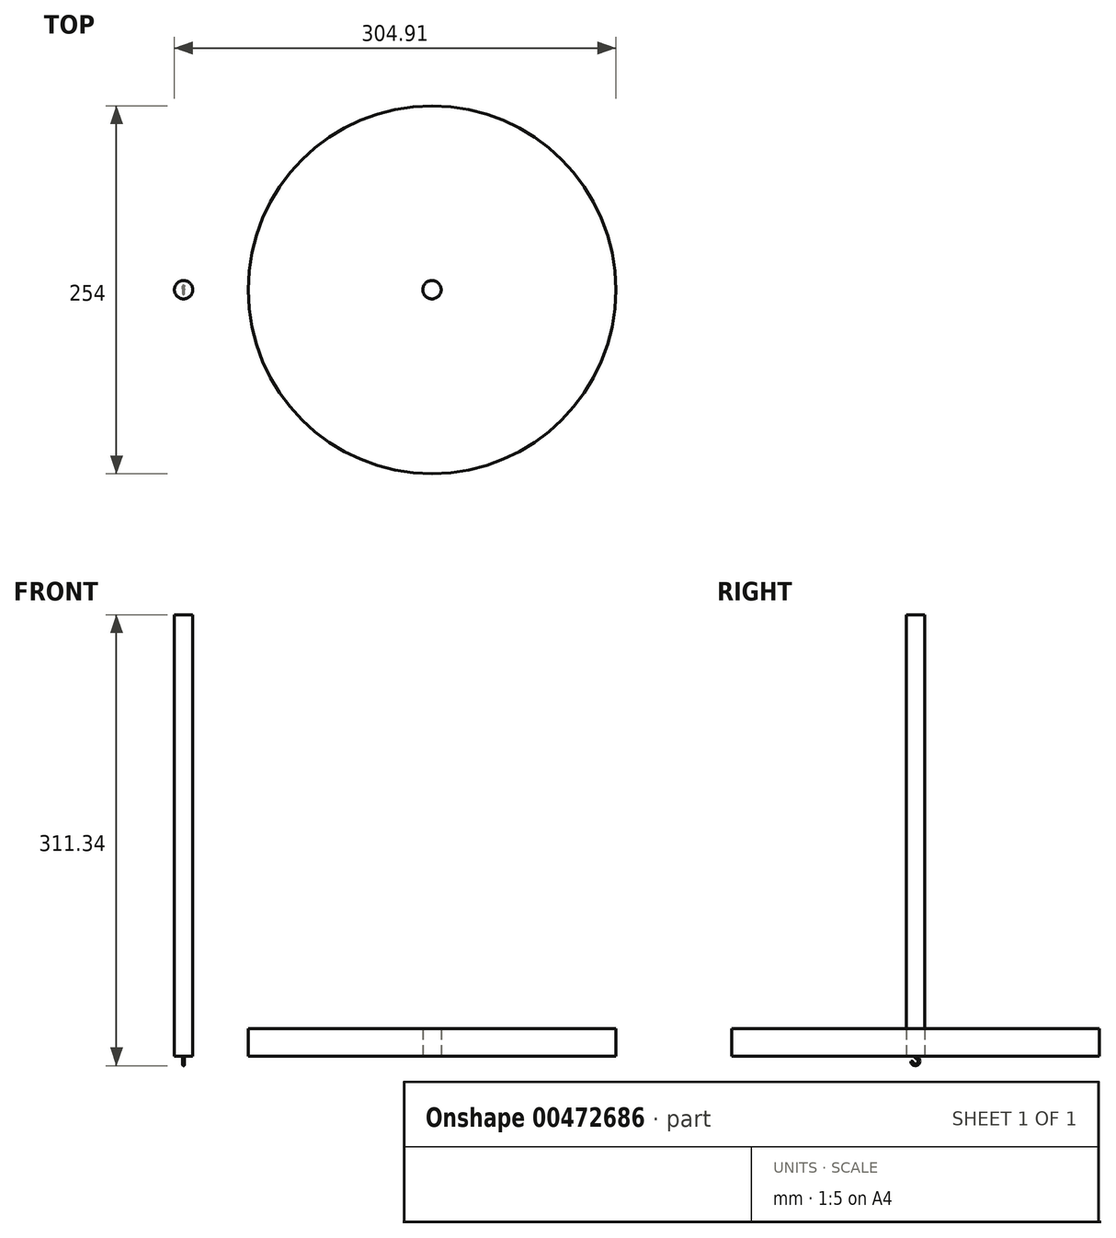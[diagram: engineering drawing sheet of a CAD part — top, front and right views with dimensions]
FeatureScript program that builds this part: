
annotation { "Feature Type Name" : "Feature", "Feature Type Description" : "" }
export const myFeature = defineFeature(function(context is Context, id is Id, definition is map)
    precondition{}
    {
        {
            var Q0;
            Q0=qCreatedBy(makeId("Top.planeOp"),FACE);
            var sketch = newSketch(context, id + "F0", { "sketchPlane" : qUnion([Q0])});
            skCircle(sketch, "E0", {"center": v(0, 0) * mm, "radius": 6.35 * mm});
            skCircle(sketch, "E1", {"center": v(171.56, 0) * mm, "radius": 127 * mm});
            skCircle(sketch, "E2", {"center": v(171.56, 0) * mm, "radius": 6.35 * mm});
            skSolve(sketch);
        }
        {
            var Q0;
            Q0=makeQuery(id+"F0.imprint","IMPRINT",FACE,{"disambiguationData":[TD([[makeQuery(id+"F0.imprint","IMPRINT",EDGE,{"derivedFrom":sQuery(id+"F0.wireOp",EDGE,"E0")}),1.0]])]});
            extrude(context, id + "F1", {"entities" : qUnion([Q0]), "depth" : 304.8 * mm, "offsetDistance" : 25.4 * mm});
        }
        {
            var Q0;
            Q0=makeQuery(id+"F0.imprint","IMPRINT",FACE,{"disambiguationData":[TD([[makeQuery(id+"F0.imprint","IMPRINT",EDGE,{"derivedFrom":sQuery(id+"F0.wireOp",EDGE,"E1")}),1.0]])]});
            extrude(context, id + "F2", {"entities" : qUnion([Q0]), "depth" : 19.05 * mm, "offsetDistance" : 25.4 * mm});
        }
        {
            var Q0;
            Q0=qCreatedBy(makeId("Right.planeOp"),FACE);
            var sketch = newSketch(context, id + "F3", { "sketchPlane" : qUnion([Q0])});
            skLineSegment(sketch, "E3", {"start": v(0, 0) * mm, "end": v(0, -0.25) * mm});
            skArc(sketch, "E4", {"start": v(-2.54, -3.36) * mm, "mid": v(1.6, -5.33) * mm, "end": v(0.5, -0.88) * mm});
            skLineSegment(sketch, "E5", {"start": v(0, -3.36) * mm, "end": v(-4.5, -3.36) * mm, "construction": true});
            skPoint(sketch, "E6.visualSharp", {"position": v(0, -0.82) * mm});
            skArc(sketch, "E6.filletArc", {"start": v(0, -0.25) * mm, "mid": v(0.14, -0.66) * mm, "end": v(0.5, -0.88) * mm});
            skSolve(sketch);
        }
        {
            var Q0;
            Q0=makeQuery(id+"F0.imprint","IMPRINT",FACE,{"disambiguationData":[TD([[makeQuery(id+"F0.imprint","IMPRINT",EDGE,{"derivedFrom":sQuery(id+"F0.wireOp",EDGE,"E0")}),1.0]])]});
            var sketch = newSketch(context, id + "F4", { "sketchPlane" : qUnion([Q0])});
            skCircle(sketch, "E7", {"center": v(0, 0) * mm, "radius": 0.64 * mm});
            skSolve(sketch);
        }
        {
            var Q0;
            Q0 = qSketchRegion(id + "F4", true);
            var Q1;
            Q1 = qConstructionFilter(qBodyType(qCreatedBy(id + "F3" ,EDGE), BodyType.WIRE), ConstructionObject.NO);
            sweep(context, id + "F5", {"operationType" : NewBodyOperationType.ADD, "profiles" : qUnion([Q0]), "path" : qUnion([Q1])});
        }
    });
